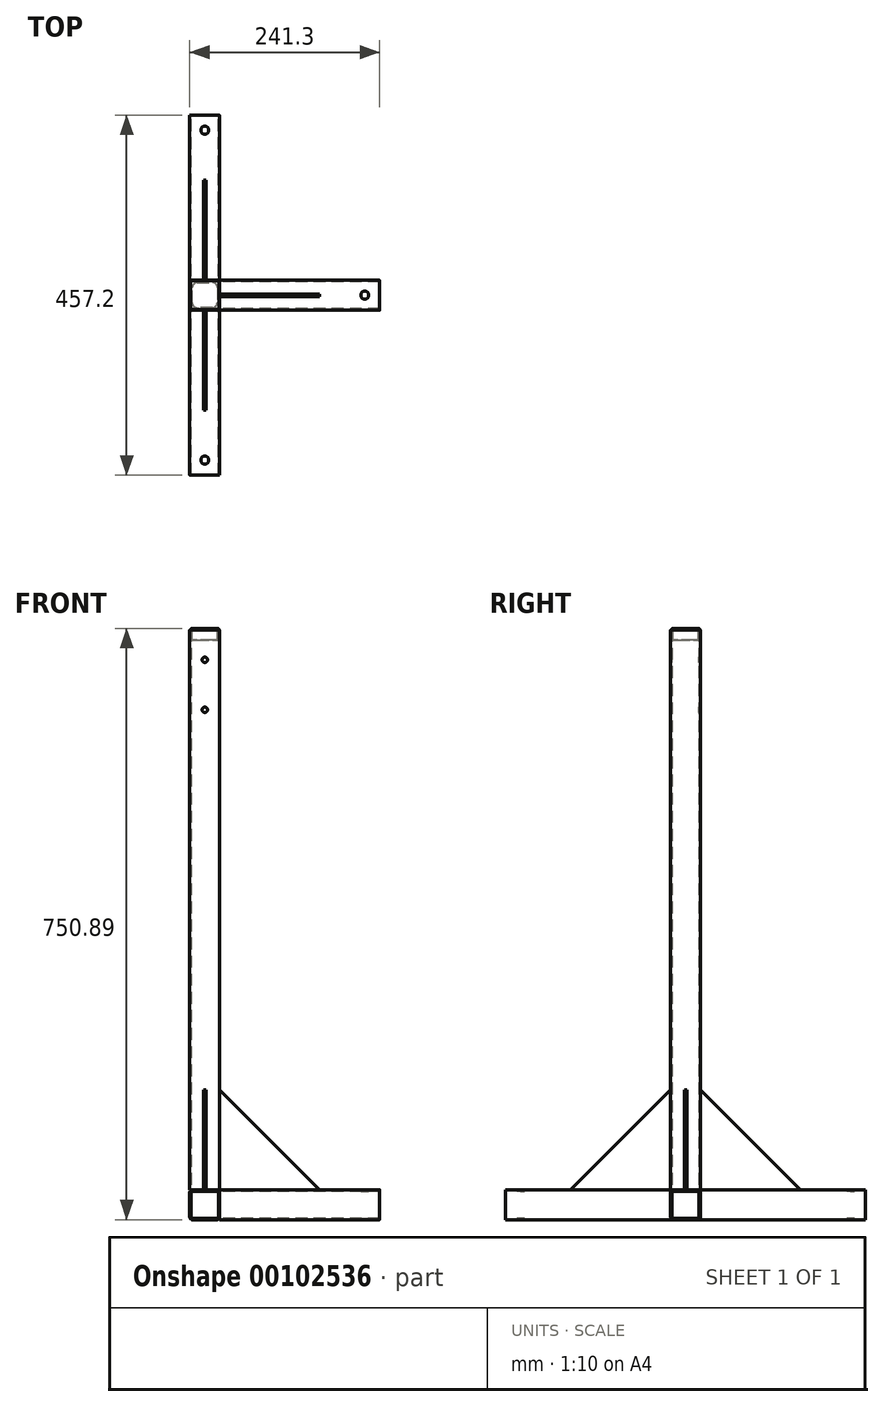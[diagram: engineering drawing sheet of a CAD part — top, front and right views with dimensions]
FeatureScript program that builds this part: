
annotation { "Feature Type Name" : "Feature", "Feature Type Description" : "" }
export const myFeature = defineFeature(function(context is Context, id is Id, definition is map)
    precondition{}
    {
        {
            var Q0;
            Q0=qCreatedBy(makeId("Front.planeOp"),FACE);
            var sketch = newSketch(context, id + "F0", { "sketchPlane" : qUnion([Q0])});
            skLineSegment(sketch, "E0.bottom", {"start": v(15.87, 0) * mm, "end": v(-15.88, 0) * mm});
            skLineSegment(sketch, "E0.top", {"start": v(15.87, 38.1) * mm, "end": v(-15.87, 38.1) * mm});
            skLineSegment(sketch, "E0.left", {"start": v(19.05, 3.18) * mm, "end": v(19.05, 34.92) * mm});
            skLineSegment(sketch, "E0.right", {"start": v(-19.05, 3.18) * mm, "end": v(-19.05, 34.92) * mm});
            skPoint(sketch, "E0.middle", {"position": v(0, 19.05) * mm});
            skPoint(sketch, "E1.visualSharp", {"position": v(-19.05, 38.1) * mm});
            skArc(sketch, "E1.filletArc", {"start": v(-15.87, 38.1) * mm, "mid": v(-18.12, 37.17) * mm, "end": v(-19.05, 34.92) * mm});
            skPoint(sketch, "E2.visualSharp", {"position": v(19.05, 38.1) * mm});
            skArc(sketch, "E2.filletArc", {"start": v(19.05, 34.92) * mm, "mid": v(18.12, 37.17) * mm, "end": v(15.87, 38.1) * mm});
            skPoint(sketch, "E3.visualSharp", {"position": v(19.05, 0) * mm});
            skArc(sketch, "E3.filletArc", {"start": v(15.87, 0) * mm, "mid": v(18.12, 0.93) * mm, "end": v(19.05, 3.18) * mm});
            skPoint(sketch, "E4.visualSharp", {"position": v(-19.05, 0) * mm});
            skArc(sketch, "E4.filletArc", {"start": v(-19.05, 3.18) * mm, "mid": v(-18.12, 0.93) * mm, "end": v(-15.88, 0) * mm});
            skArc(sketch, "E5.0", {"start": v(17.15, 34.92) * mm, "mid": v(16.78, 35.83) * mm, "end": v(15.87, 36.2) * mm});
            skLineSegment(sketch, "E5.1", {"start": v(17.15, 3.18) * mm, "end": v(17.15, 34.92) * mm});
            skLineSegment(sketch, "E5.2", {"start": v(15.87, 36.2) * mm, "end": v(-15.87, 36.2) * mm});
            skArc(sketch, "E5.3", {"start": v(15.87, 1.9) * mm, "mid": v(16.78, 2.27) * mm, "end": v(17.15, 3.18) * mm});
            skArc(sketch, "E5.4", {"start": v(-15.87, 36.2) * mm, "mid": v(-16.78, 35.83) * mm, "end": v(-17.15, 34.92) * mm});
            skLineSegment(sketch, "E5.5", {"start": v(-17.15, 3.18) * mm, "end": v(-17.15, 34.92) * mm});
            skArc(sketch, "E5.6", {"start": v(-17.15, 3.18) * mm, "mid": v(-16.78, 2.27) * mm, "end": v(-15.88, 1.9) * mm});
            skLineSegment(sketch, "E5.7", {"start": v(15.87, 1.9) * mm, "end": v(-15.88, 1.9) * mm});
            skSolve(sketch);
        }
        {
            var Q0;
            Q0 = qSketchRegion(id + "F0", true);
            extrude(context, id + "F1", {"entities" : qUnion([Q0]), "endBound" : BoundingType.SYMMETRIC, "depth" : 457.2 * mm});
        }
        {
            var Q0;
            Q0=makeQuery(id+"F1.opExtrude","SWEPT_FACE",FACE,{"disambiguationData":[OSD([sQuery(id+"F0.wireOp",EDGE,"E0.top")])]});
            var sketch = newSketch(context, id + "F2", { "sketchPlane" : qUnion([Q0])});
            skLineSegment(sketch, "E6.bottom", {"start": v(15.87, 19.05) * mm, "end": v(-15.88, 19.05) * mm});
            skLineSegment(sketch, "E6.top", {"start": v(15.87, -19.05) * mm, "end": v(-15.88, -19.05) * mm});
            skLineSegment(sketch, "E6.left", {"start": v(19.05, 15.87) * mm, "end": v(19.05, -15.87) * mm});
            skLineSegment(sketch, "E6.right", {"start": v(-19.05, 15.87) * mm, "end": v(-19.05, -15.87) * mm});
            skPoint(sketch, "E6.middle", {"position": v(0, 0) * mm});
            skPoint(sketch, "E7.visualSharp", {"position": v(-19.05, 19.05) * mm});
            skArc(sketch, "E7.filletArc", {"start": v(-15.88, 19.05) * mm, "mid": v(-18.12, 18.12) * mm, "end": v(-19.05, 15.87) * mm});
            skPoint(sketch, "E8.visualSharp", {"position": v(19.05, 19.05) * mm});
            skArc(sketch, "E8.filletArc", {"start": v(19.05, 15.87) * mm, "mid": v(18.12, 18.12) * mm, "end": v(15.87, 19.05) * mm});
            skPoint(sketch, "E9.visualSharp", {"position": v(19.05, -19.05) * mm});
            skArc(sketch, "E9.filletArc", {"start": v(15.87, -19.05) * mm, "mid": v(18.12, -18.12) * mm, "end": v(19.05, -15.87) * mm});
            skPoint(sketch, "E10.visualSharp", {"position": v(-19.05, -19.05) * mm});
            skArc(sketch, "E10.filletArc", {"start": v(-19.05, -15.87) * mm, "mid": v(-18.12, -18.12) * mm, "end": v(-15.88, -19.05) * mm});
            skArc(sketch, "E11.0", {"start": v(17.15, 15.88) * mm, "mid": v(16.78, 16.78) * mm, "end": v(15.87, 17.15) * mm});
            skLineSegment(sketch, "E11.1", {"start": v(17.15, 15.88) * mm, "end": v(17.15, -15.87) * mm});
            skLineSegment(sketch, "E11.2", {"start": v(15.87, 17.15) * mm, "end": v(-15.88, 17.15) * mm});
            skArc(sketch, "E11.3", {"start": v(15.87, -17.15) * mm, "mid": v(16.78, -16.78) * mm, "end": v(17.15, -15.87) * mm});
            skArc(sketch, "E11.4", {"start": v(-15.88, 17.15) * mm, "mid": v(-16.78, 16.78) * mm, "end": v(-17.15, 15.88) * mm});
            skLineSegment(sketch, "E11.5", {"start": v(-17.15, 15.87) * mm, "end": v(-17.15, -15.87) * mm});
            skArc(sketch, "E11.6", {"start": v(-17.15, -15.87) * mm, "mid": v(-16.78, -16.78) * mm, "end": v(-15.88, -17.15) * mm});
            skLineSegment(sketch, "E11.7", {"start": v(15.87, -17.15) * mm, "end": v(-15.88, -17.15) * mm});
            skSolve(sketch);
        }
        {
            var Q0;
            Q0 = qSketchRegion(id + "F2", true);
            extrude(context, id + "F3", {"entities" : qUnion([Q0]), "depth" : 711.2 * mm});
        }
        {
            var Q0;
            Q0=qCreatedBy(makeId("Right.planeOp"),FACE);
            var sketch = newSketch(context, id + "F4", { "sketchPlane" : qUnion([Q0])});
            skLineSegment(sketch, "E12", {"start": v(19.05, 165.1) * mm, "end": v(146.05, 38.1) * mm});
            skLineSegment(sketch, "E13", {"start": v(146.05, 38.1) * mm, "end": v(19.05, 38.1) * mm});
            skLineSegment(sketch, "E14", {"start": v(19.05, 38.1) * mm, "end": v(19.05, 165.1) * mm});
            skLineSegment(sketch, "E15", {"start": v(0, 0) * mm, "end": v(0, 75.99) * mm, "construction": true});
            skSolve(sketch);
        }
        {
            var Q0;
            Q0 = qSketchRegion(id + "F4", true);
            extrude(context, id + "F5", {"entities" : qUnion([Q0]), "endBound" : BoundingType.SYMMETRIC, "depth" : 3.17 * mm});
        }
        {
            var Q0;
            Q0=makeQuery(id+"F5.opExtrude","SWEPT_BODY",BODY,{"disambiguationData":[OSD([sQuery(id+"F4.wireOp",EDGE,"E12"),sQuery(id+"F4.wireOp",EDGE,"E13"),sQuery(id+"F4.wireOp",EDGE,"E14")])]});
            var Q1;
            Q1=qCreatedBy(makeId("Front.planeOp"),FACE);
            mirror(context, id + "F6", {"entities" : qUnion([Q0]), "mirrorPlane" : qUnion([Q1])});
        }
        {
            var Q0;
            Q0=makeQuery(id+"F1.opExtrude","SWEPT_FACE",FACE,{"disambiguationData":[OSD([sQuery(id+"F0.wireOp",EDGE,"E0.top")])]});
            var sketch = newSketch(context, id + "F7", { "sketchPlane" : qUnion([Q0])});
            skPoint(sketch, "E16", {"position": v(0, -209.55) * mm});
            skLineSegment(sketch, "E17", {"start": v(0, 0) * mm, "end": v(95.48, 0) * mm, "construction": true});
            skPoint(sketch, "E18.MirrorP", {"position": v(0, 209.55) * mm});
            skSolve(sketch);
        }
        {
            var Q0;
            Q0=makeQuery(id+"F3.opExtrude","SWEPT_FACE",FACE,{"disambiguationData":[OSD([sQuery(id+"F2.wireOp",EDGE,"E6.top")])]});
            var sketch = newSketch(context, id + "F8", { "sketchPlane" : qUnion([Q0])});
            skPoint(sketch, "E19", {"position": v(0, 711.2) * mm});
            skPoint(sketch, "E20", {"position": v(0, 647.7) * mm});
            skSolve(sketch);
        }
        {
            var Q0;
            Q0=sQuery(id+"F8.wireOp",VERTEX,"E19");
            var Q1;
            Q1=sQuery(id+"F8.wireOp",VERTEX,"E20");
            var Q2;
            Q2=makeQuery(id+"F3.opExtrude","SWEPT_BODY",BODY,{"disambiguationData":[OSD([sQuery(id+"F2.wireOp",EDGE,"E6.bottom"),sQuery(id+"F2.wireOp",EDGE,"E6.top"),sQuery(id+"F2.wireOp",EDGE,"E6.left"),sQuery(id+"F2.wireOp",EDGE,"E6.right"),sQuery(id+"F2.wireOp",EDGE,"E7.filletArc"),sQuery(id+"F2.wireOp",EDGE,"E8.filletArc"),sQuery(id+"F2.wireOp",EDGE,"E9.filletArc"),sQuery(id+"F2.wireOp",EDGE,"E10.filletArc"),sQuery(id+"F2.wireOp",EDGE,"E11.0"),sQuery(id+"F2.wireOp",EDGE,"E11.1"),sQuery(id+"F2.wireOp",EDGE,"E11.2"),sQuery(id+"F2.wireOp",EDGE,"E11.3"),sQuery(id+"F2.wireOp",EDGE,"E11.4"),sQuery(id+"F2.wireOp",EDGE,"E11.5"),sQuery(id+"F2.wireOp",EDGE,"E11.6"),sQuery(id+"F2.wireOp",EDGE,"E11.7")])]});
            hole(context, id + "F9", {"style" : HoleStyle.SIMPLE, "endStyle" : HoleEndStyle.THROUGH, "standardTappedOrClearance" : lookupTablePath({ "standard" : "ANSI", "fit" : "Normal (ASME)", "size" : "1/4", "type" : "Clearance" }), "standardBlindInLast" : lookupTablePath({ "fit" : "Free", "standard" : "ANSI", "size" : "1/4", "type" : "Clearance" }), "holeDiameter" : 6.76 * mm, "locations" : qUnion([Q0, Q1]), "scope" : qUnion([Q2]), "isTappedThrough" : true});
        }
        {
            var Q0;
            Q0=makeQuery(id+"F3.opExtrude","CAP_FACE",FACE,{"disambiguationData":[OSD([sQuery(id+"F2.wireOp",EDGE,"E6.bottom"),sQuery(id+"F2.wireOp",EDGE,"E6.top"),sQuery(id+"F2.wireOp",EDGE,"E6.left"),sQuery(id+"F2.wireOp",EDGE,"E6.right"),sQuery(id+"F2.wireOp",EDGE,"E7.filletArc"),sQuery(id+"F2.wireOp",EDGE,"E8.filletArc"),sQuery(id+"F2.wireOp",EDGE,"E9.filletArc"),sQuery(id+"F2.wireOp",EDGE,"E10.filletArc"),sQuery(id+"F2.wireOp",EDGE,"E11.0"),sQuery(id+"F2.wireOp",EDGE,"E11.1"),sQuery(id+"F2.wireOp",EDGE,"E11.2"),sQuery(id+"F2.wireOp",EDGE,"E11.3"),sQuery(id+"F2.wireOp",EDGE,"E11.4"),sQuery(id+"F2.wireOp",EDGE,"E11.5"),sQuery(id+"F2.wireOp",EDGE,"E11.6"),sQuery(id+"F2.wireOp",EDGE,"E11.7")])],"isStart":false});
            var sketch = newSketch(context, id + "F10", { "sketchPlane" : qUnion([Q0])});
            skLineSegment(sketch, "E21.bottom", {"start": v(15.88, 18.26) * mm, "end": v(-15.88, 18.26) * mm});
            skLineSegment(sketch, "E21.top", {"start": v(15.88, -18.26) * mm, "end": v(-15.88, -18.26) * mm});
            skLineSegment(sketch, "E21.left", {"start": v(18.26, 15.87) * mm, "end": v(18.26, -15.87) * mm});
            skLineSegment(sketch, "E21.right", {"start": v(-18.26, 15.88) * mm, "end": v(-18.26, -15.87) * mm});
            skPoint(sketch, "E21.middle", {"position": v(0, 0) * mm});
            skPoint(sketch, "E22.visualSharp", {"position": v(-18.26, 18.26) * mm});
            skArc(sketch, "E22.filletArc", {"start": v(-15.88, 18.26) * mm, "mid": v(-17.56, 17.56) * mm, "end": v(-18.26, 15.88) * mm});
            skPoint(sketch, "E23.visualSharp", {"position": v(18.26, 18.26) * mm});
            skArc(sketch, "E23.filletArc", {"start": v(18.26, 15.87) * mm, "mid": v(17.56, 17.56) * mm, "end": v(15.88, 18.26) * mm});
            skPoint(sketch, "E24.visualSharp", {"position": v(18.26, -18.26) * mm});
            skArc(sketch, "E24.filletArc", {"start": v(15.88, -18.26) * mm, "mid": v(17.56, -17.56) * mm, "end": v(18.26, -15.87) * mm});
            skPoint(sketch, "E25.visualSharp", {"position": v(-18.26, -18.26) * mm});
            skArc(sketch, "E25.filletArc", {"start": v(-18.26, -15.87) * mm, "mid": v(-17.56, -17.56) * mm, "end": v(-15.88, -18.26) * mm});
            skSolve(sketch);
        }
        {
            var Q0;
            Q0 = qSketchRegion(id + "F10", true);
            extrude(context, id + "F11", {"entities" : qUnion([Q0]), "depth" : 1.59 * mm});
        }
        {
            var Q0;
            Q0=makeQuery(id+"F11.opExtrude","CAP_EDGE",EDGE,{"disambiguationData":[OSD([sQuery(id+"F10.wireOp",EDGE,"E21.top")])],"isStart":false});
            fillet(context, id + "F12", {"entities" : qUnion([Q0]), "radius" : 1.59 * mm, "tangentPropagation" : true, "allowEdgeOverflow" : false});
        }
        {
            var Q0;
            Q0=makeQuery(id+"F11.opExtrude","CAP_FACE",FACE,{"disambiguationData":[OSD([sQuery(id+"F10.wireOp",EDGE,"E21.bottom"),sQuery(id+"F10.wireOp",EDGE,"E21.top"),sQuery(id+"F10.wireOp",EDGE,"E21.left"),sQuery(id+"F10.wireOp",EDGE,"E21.right"),sQuery(id+"F10.wireOp",EDGE,"E22.filletArc"),sQuery(id+"F10.wireOp",EDGE,"E23.filletArc"),sQuery(id+"F10.wireOp",EDGE,"E24.filletArc"),sQuery(id+"F10.wireOp",EDGE,"E25.filletArc")])],"isStart":true});
            var sketch = newSketch(context, id + "F13", { "sketchPlane" : qUnion([Q0])});
            skLineSegment(sketch, "E26.0", {"start": v(-9.6, -15.9) * mm, "end": v(9.7, -15.96) * mm});
            skLineSegment(sketch, "E26.3", {"start": v(-16.08, 9.56) * mm, "end": v(-15.93, -9.6) * mm});
            skLineSegment(sketch, "E26.4", {"start": v(16.08, -9.56) * mm, "end": v(15.93, 9.6) * mm});
            skLineSegment(sketch, "E26.6", {"start": v(9.6, 15.9) * mm, "end": v(-9.7, 15.96) * mm});
            skPoint(sketch, "E27.visualSharp", {"position": v(-16.13, 15.99) * mm});
            skArc(sketch, "E27.filletArc", {"start": v(-9.7, 15.96) * mm, "mid": v(-14.23, 14.1) * mm, "end": v(-16.08, 9.56) * mm});
            skPoint(sketch, "E28.visualSharp", {"position": v(-15.88, -15.87) * mm});
            skArc(sketch, "E28.filletArc", {"start": v(-15.93, -9.6) * mm, "mid": v(-14.06, -14.05) * mm, "end": v(-9.6, -15.9) * mm});
            skPoint(sketch, "E29.visualSharp", {"position": v(16.13, -15.99) * mm});
            skArc(sketch, "E29.filletArc", {"start": v(9.7, -15.96) * mm, "mid": v(14.23, -14.1) * mm, "end": v(16.08, -9.56) * mm});
            skPoint(sketch, "E30.visualSharp", {"position": v(15.88, 15.88) * mm});
            skArc(sketch, "E30.filletArc", {"start": v(15.93, 9.6) * mm, "mid": v(14.06, 14.05) * mm, "end": v(9.6, 15.9) * mm});
            skSolve(sketch);
        }
        {
            var Q0;
            Q0 = qSketchRegion(id + "F13", true);
            extrude(context, id + "F14", {"entities" : qUnion([Q0]), "operationType" : NewBodyOperationType.ADD, "depth" : 12.7 * mm});
        }
        {
            var Q0;
            Q0=makeQuery(id+"F1.opExtrude","SWEPT_FACE",FACE,{"disambiguationData":[OSD([sQuery(id+"F0.wireOp",EDGE,"E0.left")])]});
            var sketch = newSketch(context, id + "F15", { "sketchPlane" : qUnion([Q0])});
            skLineSegment(sketch, "E31.bottom", {"start": v(15.87, 38.1) * mm, "end": v(-15.88, 38.1) * mm});
            skLineSegment(sketch, "E31.top", {"start": v(15.88, 0) * mm, "end": v(-15.88, 0) * mm});
            skLineSegment(sketch, "E31.left", {"start": v(19.05, 34.92) * mm, "end": v(19.05, 3.17) * mm});
            skLineSegment(sketch, "E31.right", {"start": v(-19.05, 34.93) * mm, "end": v(-19.05, 3.17) * mm});
            skPoint(sketch, "E31.middle", {"position": v(0, 19.05) * mm});
            skPoint(sketch, "E32.visualSharp", {"position": v(19.05, 38.1) * mm});
            skArc(sketch, "E32.filletArc", {"start": v(19.05, 34.92) * mm, "mid": v(18.12, 37.17) * mm, "end": v(15.87, 38.1) * mm});
            skPoint(sketch, "E33.visualSharp", {"position": v(19.05, 0) * mm});
            skArc(sketch, "E33.filletArc", {"start": v(15.88, 0) * mm, "mid": v(18.12, 0.93) * mm, "end": v(19.05, 3.17) * mm});
            skPoint(sketch, "E34.visualSharp", {"position": v(-19.05, 0) * mm});
            skArc(sketch, "E34.filletArc", {"start": v(-19.05, 3.17) * mm, "mid": v(-18.12, 0.93) * mm, "end": v(-15.88, 0) * mm});
            skPoint(sketch, "E35.visualSharp", {"position": v(-19.05, 38.1) * mm});
            skArc(sketch, "E35.filletArc", {"start": v(-15.88, 38.1) * mm, "mid": v(-18.12, 37.17) * mm, "end": v(-19.05, 34.93) * mm});
            skArc(sketch, "E36.0", {"start": v(17.15, 34.92) * mm, "mid": v(16.78, 35.83) * mm, "end": v(15.87, 36.2) * mm});
            skLineSegment(sketch, "E36.1", {"start": v(17.15, 34.92) * mm, "end": v(17.15, 3.17) * mm});
            skLineSegment(sketch, "E36.2", {"start": v(15.87, 36.2) * mm, "end": v(-15.88, 36.2) * mm});
            skArc(sketch, "E36.3", {"start": v(15.88, 1.9) * mm, "mid": v(16.78, 2.27) * mm, "end": v(17.15, 3.17) * mm});
            skArc(sketch, "E36.4", {"start": v(-15.88, 36.2) * mm, "mid": v(-16.78, 35.83) * mm, "end": v(-17.15, 34.93) * mm});
            skLineSegment(sketch, "E36.5", {"start": v(-17.15, 34.93) * mm, "end": v(-17.15, 3.17) * mm});
            skArc(sketch, "E36.6", {"start": v(-17.15, 3.17) * mm, "mid": v(-16.78, 2.27) * mm, "end": v(-15.88, 1.9) * mm});
            skLineSegment(sketch, "E36.7", {"start": v(15.88, 1.9) * mm, "end": v(-15.88, 1.9) * mm});
            skSolve(sketch);
        }
        {
            var Q0;
            Q0 = qSketchRegion(id + "F15", true);
            extrude(context, id + "F16", {"entities" : qUnion([Q0]), "depth" : 203.2 * mm});
        }
        {
            var Q0;
            Q0=sQuery(id+"F7.wireOp",VERTEX,"E16");
            var Q1;
            Q1=sQuery(id+"F7.wireOp",VERTEX,"E18.MirrorP");
            var Q2;
            Q2=makeQuery(id+"F1.opExtrude","SWEPT_BODY",BODY,{"disambiguationData":[OSD([sQuery(id+"F0.wireOp",EDGE,"E0.bottom"),sQuery(id+"F0.wireOp",EDGE,"E0.top"),sQuery(id+"F0.wireOp",EDGE,"E0.left"),sQuery(id+"F0.wireOp",EDGE,"E0.right"),sQuery(id+"F0.wireOp",EDGE,"E1.filletArc"),sQuery(id+"F0.wireOp",EDGE,"E2.filletArc"),sQuery(id+"F0.wireOp",EDGE,"E3.filletArc"),sQuery(id+"F0.wireOp",EDGE,"E4.filletArc"),sQuery(id+"F0.wireOp",EDGE,"E5.0"),sQuery(id+"F0.wireOp",EDGE,"E5.1"),sQuery(id+"F0.wireOp",EDGE,"E5.2"),sQuery(id+"F0.wireOp",EDGE,"E5.3"),sQuery(id+"F0.wireOp",EDGE,"E5.4"),sQuery(id+"F0.wireOp",EDGE,"E5.5"),sQuery(id+"F0.wireOp",EDGE,"E5.6"),sQuery(id+"F0.wireOp",EDGE,"E5.7")])]});
            hole(context, id + "F17", {"style" : HoleStyle.SIMPLE, "endStyle" : HoleEndStyle.THROUGH, "standardTappedOrClearance" : lookupTablePath({ "standard" : "ANSI", "fit" : "Normal (ASME)", "size" : "3/8", "type" : "Clearance" }), "standardBlindInLast" : lookupTablePath({ "fit" : "Free", "standard" : "ANSI", "size" : "3/8", "type" : "Clearance" }), "holeDiameter" : 10.08 * mm, "locations" : qUnion([Q0, Q1]), "scope" : qUnion([Q2]), "isTappedThrough" : true});
        }
        {
            var Q0;
            Q0=makeQuery(id+"F16.opExtrude","SWEPT_FACE",FACE,{"disambiguationData":[OSD([sQuery(id+"F15.wireOp",EDGE,"E31.bottom")])]});
            var sketch = newSketch(context, id + "F18", { "sketchPlane" : qUnion([Q0])});
            skPoint(sketch, "E37", {"position": v(203.2, 0) * mm});
            skLineSegment(sketch, "E38", {"start": v(222.25, 0) * mm, "end": v(203.2, 0) * mm, "construction": true});
            skSolve(sketch);
        }
        {
            var Q0;
            Q0=sQuery(id+"F18.wireOp",VERTEX,"E37");
            var Q1;
            Q1=makeQuery(id+"F16.opExtrude","SWEPT_BODY",BODY,{"disambiguationData":[OSD([sQuery(id+"F15.wireOp",EDGE,"E31.bottom"),sQuery(id+"F15.wireOp",EDGE,"E31.top"),sQuery(id+"F15.wireOp",EDGE,"E31.left"),sQuery(id+"F15.wireOp",EDGE,"E31.right"),sQuery(id+"F15.wireOp",EDGE,"E32.filletArc"),sQuery(id+"F15.wireOp",EDGE,"E33.filletArc"),sQuery(id+"F15.wireOp",EDGE,"E34.filletArc"),sQuery(id+"F15.wireOp",EDGE,"E35.filletArc"),sQuery(id+"F15.wireOp",EDGE,"E36.0"),sQuery(id+"F15.wireOp",EDGE,"E36.1"),sQuery(id+"F15.wireOp",EDGE,"E36.2"),sQuery(id+"F15.wireOp",EDGE,"E36.3"),sQuery(id+"F15.wireOp",EDGE,"E36.4"),sQuery(id+"F15.wireOp",EDGE,"E36.5"),sQuery(id+"F15.wireOp",EDGE,"E36.6"),sQuery(id+"F15.wireOp",EDGE,"E36.7")])]});
            hole(context, id + "F19", {"style" : HoleStyle.SIMPLE, "endStyle" : HoleEndStyle.THROUGH, "standardTappedOrClearance" : lookupTablePath({ "standard" : "ANSI", "fit" : "Normal (ASME)", "size" : "3/8", "type" : "Clearance" }), "standardBlindInLast" : lookupTablePath({ "fit" : "Free", "standard" : "ANSI", "size" : "3/8", "type" : "Clearance" }), "holeDiameter" : 10.08 * mm, "locations" : qUnion([Q0]), "scope" : qUnion([Q1]), "isTappedThrough" : true});
        }
        {
            var Q0;
            Q0=makeQuery(id+"F5.opExtrude","SWEPT_BODY",BODY,{"disambiguationData":[OSD([sQuery(id+"F4.wireOp",EDGE,"E12"),sQuery(id+"F4.wireOp",EDGE,"E13"),sQuery(id+"F4.wireOp",EDGE,"E14")])]});
            var Q1;
            Q1=sQuery(id+"F4.wireOp",EDGE,"E15");
            transform(context, id + "F20", {"entities" : qUnion([Q0]), "transformType" : TransformType.ROTATION, "transformAxis" : qUnion([Q1]), "angle" : 270 * degree, "makeCopy" : true});
        }
    });
